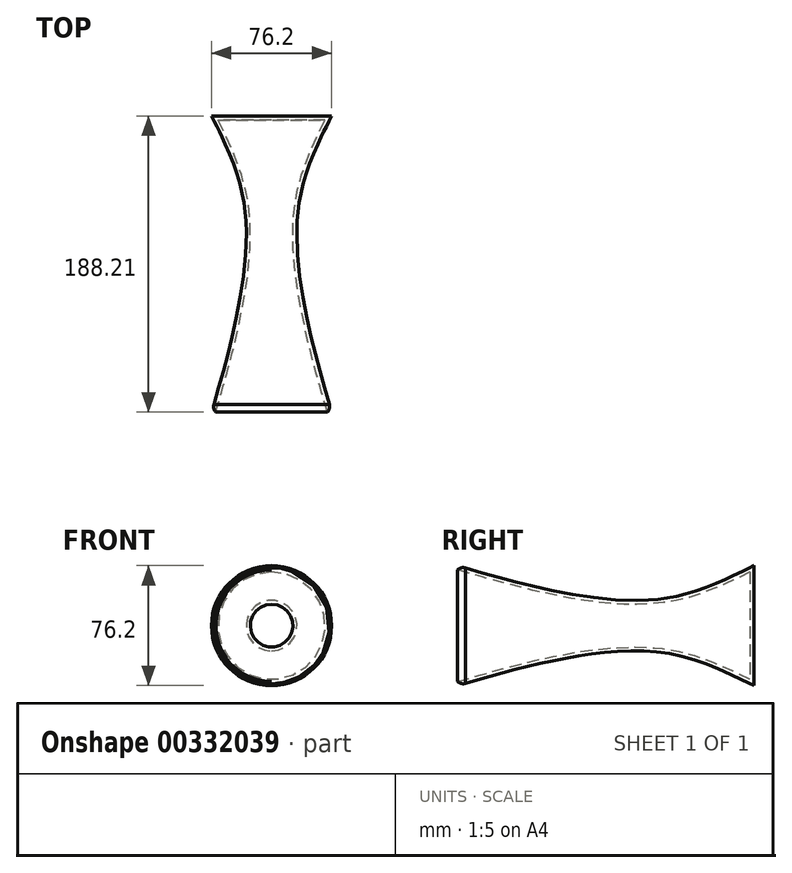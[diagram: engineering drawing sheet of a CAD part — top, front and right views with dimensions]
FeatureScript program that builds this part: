
annotation { "Feature Type Name" : "Feature", "Feature Type Description" : "" }
export const myFeature = defineFeature(function(context is Context, id is Id, definition is map)
    precondition{}
    {
        {
            var Q0;
            Q0=qCreatedBy(makeId("Front.planeOp"),FACE);
            cPlane(context, id + "F0", {"entities" : qUnion([Q0]), "cplaneType" : CPlaneType.OFFSET, "offset" : 47.24 * mm, "width" : 152.4 * mm, "height" : 152.4 * mm});
        }
        {
            var Q0;
            Q0=qCreatedBy(id+"F0.planeOp",FACE);
            cPlane(context, id + "F1", {"entities" : qUnion([Q0]), "cplaneType" : CPlaneType.OFFSET, "offset" : 63 * mm, "width" : 152.4 * mm, "height" : 152.4 * mm});
        }
        {
            var Q0;
            Q0=qCreatedBy(id+"F1.planeOp",FACE);
            cPlane(context, id + "F2", {"entities" : qUnion([Q0]), "cplaneType" : CPlaneType.OFFSET, "offset" : 77.98 * mm, "width" : 152.4 * mm, "height" : 152.4 * mm});
        }
        {
            var Q0;
            Q0=qCreatedBy(makeId("Front.planeOp"),FACE);
            var sketch = newSketch(context, id + "F3", { "sketchPlane" : qUnion([Q0])});
            skCircle(sketch, "E0", {"center": v(0, 0) * mm, "radius": 38.1 * mm});
            skSolve(sketch);
        }
        {
            var Q0;
            Q0=qCreatedBy(id+"F0.planeOp",FACE);
            var sketch = newSketch(context, id + "F4", { "sketchPlane" : qUnion([Q0])});
            skCircle(sketch, "E1", {"center": v(0, 0) * mm, "radius": 19.05 * mm});
            skSolve(sketch);
        }
        {
            var Q0;
            Q0=qCreatedBy(id+"F1.planeOp",FACE);
            var sketch = newSketch(context, id + "F5", { "sketchPlane" : qUnion([Q0])});
            skCircle(sketch, "E2", {"center": v(0, 0) * mm, "radius": 19.05 * mm});
            skSolve(sketch);
        }
        {
            var Q0;
            Q0=qCreatedBy(id+"F2.planeOp",FACE);
            var sketch = newSketch(context, id + "F6", { "sketchPlane" : qUnion([Q0])});
            skCircle(sketch, "E3", {"center": v(0, 0) * mm, "radius": 38.1 * mm});
            skSolve(sketch);
        }
        {
            var Q0;
            Q0=makeQuery(id+"F3.imprint","IMPRINT",FACE,{"disambiguationData":[TD([[makeQuery(id+"F3.imprint","IMPRINT",EDGE,{"derivedFrom":sQuery(id+"F3.wireOp",EDGE,"E0")}),1.0]])]});
            var Q1;
            Q1=makeQuery(id+"F4.imprint","IMPRINT",FACE,{"disambiguationData":[TD([[makeQuery(id+"F4.imprint","IMPRINT",EDGE,{"derivedFrom":sQuery(id+"F4.wireOp",EDGE,"E1")}),1.0]])]});
            var Q2;
            Q2=makeQuery(id+"F5.imprint","IMPRINT",FACE,{"disambiguationData":[TD([[makeQuery(id+"F5.imprint","IMPRINT",EDGE,{"derivedFrom":sQuery(id+"F5.wireOp",EDGE,"E2")}),1.0]])]});
            var Q3;
            Q3=makeQuery(id+"F6.imprint","IMPRINT",FACE,{"disambiguationData":[TD([[makeQuery(id+"F6.imprint","IMPRINT",EDGE,{"derivedFrom":sQuery(id+"F6.wireOp",EDGE,"E3")}),1.0]])]});
            loft(context, id + "F7", {"sheetProfilesArray" : [{ "sheetProfileEntities" : qUnion([Q0]) }, { "sheetProfileEntities" : qUnion([Q1]) }, { "sheetProfileEntities" : qUnion([Q2]) }, { "sheetProfileEntities" : qUnion([Q3]) }]});
        }
        {
            var Q0;
            Q0=makeQuery(id+"F7.opLoft","CAP_FACE",FACE,{"disambiguationData":[OSD([makeQuery(id+"F6.imprint","IMPRINT",FACE,{"disambiguationData":[TD([[makeQuery(id+"F6.imprint","IMPRINT",EDGE,{"derivedFrom":sQuery(id+"F6.wireOp",EDGE,"E3")}),1.0]])]})])],"isStart":true});
            shell(context, id + "F8", {"entities" : qUnion([Q0]), "thickness" : 2.54 * mm});
        }
        {
            var Q0;
            Q0=makeQuery(id+"F7.opLoft","MID_CAP_EDGE",EDGE,{"disambiguationData":[OSD([sQuery(id+"F3.wireOp",EDGE,"E0"),sQuery(id+"F6.wireOp",EDGE,"E3")])],"capPos":3.0});
            fillet(context, id + "F9", {"entities" : qUnion([Q0]), "radius" : 5.08 * mm, "tangentPropagation" : true, "allowEdgeOverflow" : false});
        }
    });
